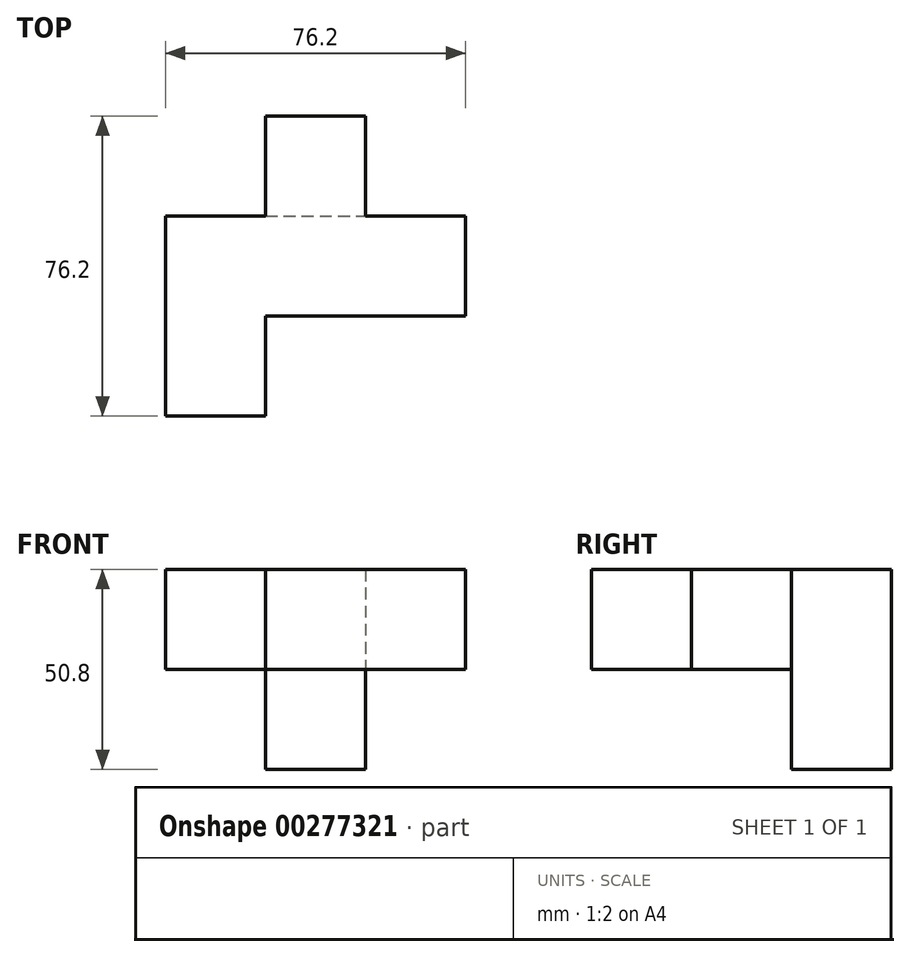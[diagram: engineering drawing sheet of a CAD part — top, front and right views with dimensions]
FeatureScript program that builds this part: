
annotation { "Feature Type Name" : "Feature", "Feature Type Description" : "" }
export const myFeature = defineFeature(function(context is Context, id is Id, definition is map)
    precondition{}
    {
        {
            var Q0;
            Q0=qCreatedBy(makeId("Front.planeOp"),FACE);
            var sketch = newSketch(context, id + "F0", { "sketchPlane" : qUnion([Q0])});
            skLineSegment(sketch, "E0", {"start": v(-44.56, 11.04) * mm, "end": v(-44.56, -14.36) * mm});
            skLineSegment(sketch, "E1", {"start": v(-44.56, -14.36) * mm, "end": v(-19.16, -14.36) * mm});
            skLineSegment(sketch, "E2", {"start": v(-19.16, -14.36) * mm, "end": v(6.24, -14.36) * mm});
            skLineSegment(sketch, "E3", {"start": v(6.24, -14.36) * mm, "end": v(31.64, -14.36) * mm});
            skLineSegment(sketch, "E4", {"start": v(31.64, -14.36) * mm, "end": v(31.64, 11.04) * mm});
            skLineSegment(sketch, "E5", {"start": v(31.64, 11.04) * mm, "end": v(6.24, 11.04) * mm});
            skLineSegment(sketch, "E6", {"start": v(6.24, 11.04) * mm, "end": v(-19.16, 11.04) * mm});
            skLineSegment(sketch, "E7", {"start": v(-19.16, 11.04) * mm, "end": v(-44.56, 11.04) * mm});
            skLineSegment(sketch, "E8", {"start": v(-19.16, 11.04) * mm, "end": v(-19.16, -14.36) * mm});
            skLineSegment(sketch, "E9", {"start": v(6.24, 11.04) * mm, "end": v(6.24, -14.36) * mm});
            skSolve(sketch);
        }
        {
            var Q0;
            Q0=makeQuery(id+"F0.imprint","IMPRINT",FACE,{"disambiguationData":[TD([[makeQuery(id+"F0.imprint","IMPRINT",EDGE,{"derivedFrom":sQuery(id+"F0.wireOp",EDGE,"E0")}),1.0]])]});
            extrude(context, id + "F1", {"entities" : qUnion([Q0]), "depth" : 50.8 * mm});
        }
        {
            var Q0;
            Q0=makeQuery(id+"F0.imprint","IMPRINT",FACE,{"disambiguationData":[TD([[makeQuery(id+"F0.imprint","IMPRINT",EDGE,{"derivedFrom":sQuery(id+"F0.wireOp",EDGE,"E3")}),1.0]])]});
            var Q1;
            Q1=makeQuery(id+"F0.imprint","IMPRINT",FACE,{"disambiguationData":[TD([[makeQuery(id+"F0.imprint","IMPRINT",EDGE,{"derivedFrom":sQuery(id+"F0.wireOp",EDGE,"E2")}),1.0]])]});
            extrude(context, id + "F2", {"entities" : qUnion([Q0, Q1]), "operationType" : NewBodyOperationType.ADD, "depth" : 25.4 * mm});
        }
        {
            var Q0;
            Q0=makeQuery(id+"F0.imprint","IMPRINT",FACE,{"disambiguationData":[TD([[makeQuery(id+"F0.imprint","IMPRINT",EDGE,{"derivedFrom":sQuery(id+"F0.wireOp",EDGE,"E2")}),1.0]])]});
            var sketch = newSketch(context, id + "F3", { "sketchPlane" : qUnion([Q0])});
            skLineSegment(sketch, "E10.bottom", {"start": v(6.24, 11.04) * mm, "end": v(-19.16, 11.04) * mm});
            skLineSegment(sketch, "E10.top", {"start": v(6.24, -14.36) * mm, "end": v(-19.16, -14.36) * mm});
            skLineSegment(sketch, "E10.left", {"start": v(6.24, 11.04) * mm, "end": v(6.24, -14.36) * mm});
            skLineSegment(sketch, "E10.right", {"start": v(-19.16, 11.04) * mm, "end": v(-19.16, -14.36) * mm});
            skSolve(sketch);
        }
        {
            var Q0;
            Q0 = qSketchRegion(id + "F3", true);
            extrude(context, id + "F4", {"entities" : qUnion([Q0]), "operationType" : NewBodyOperationType.ADD, "oppositeDirection" : true, "depth" : 25.4 * mm});
        }
        {
            var Q0;
            Q0=makeQuery(id+"F4.boolean.opBoolean","MERGE",FACE,{"derivedFrom":[makeQuery(id+"F2.boolean.opBoolean","MERGE",FACE,{"derivedFrom":[makeQuery(id+"F1.opExtrude","SWEPT_FACE",FACE,{"disambiguationData":[OSD([sQuery(id+"F0.wireOp",EDGE,"E1")])]}),makeQuery(id+"F2.opExtrude","SWEPT_FACE",FACE,{"disambiguationData":[OSD([sQuery(id+"F0.wireOp",EDGE,"E2"),sQuery(id+"F0.wireOp",EDGE,"E3")])]})]}),makeQuery(id+"F4.opExtrude","SWEPT_FACE",FACE,{"disambiguationData":[OSD([sQuery(id+"F3.wireOp",EDGE,"E10.top")])]})]});
            var sketch = newSketch(context, id + "F5", { "sketchPlane" : qUnion([Q0])});
            skLineSegment(sketch, "E11.bottom", {"start": v(-19.16, 0) * mm, "end": v(6.24, 0) * mm});
            skLineSegment(sketch, "E11.top", {"start": v(-19.16, -25.4) * mm, "end": v(6.24, -25.4) * mm});
            skLineSegment(sketch, "E11.left", {"start": v(-19.16, 0) * mm, "end": v(-19.16, -25.4) * mm});
            skLineSegment(sketch, "E11.right", {"start": v(6.24, 0) * mm, "end": v(6.24, -25.4) * mm});
            skSolve(sketch);
        }
        {
            var Q0;
            Q0 = qSketchRegion(id + "F5", true);
            extrude(context, id + "F6", {"entities" : qUnion([Q0]), "operationType" : NewBodyOperationType.ADD, "depth" : 25.4 * mm});
        }
    });
